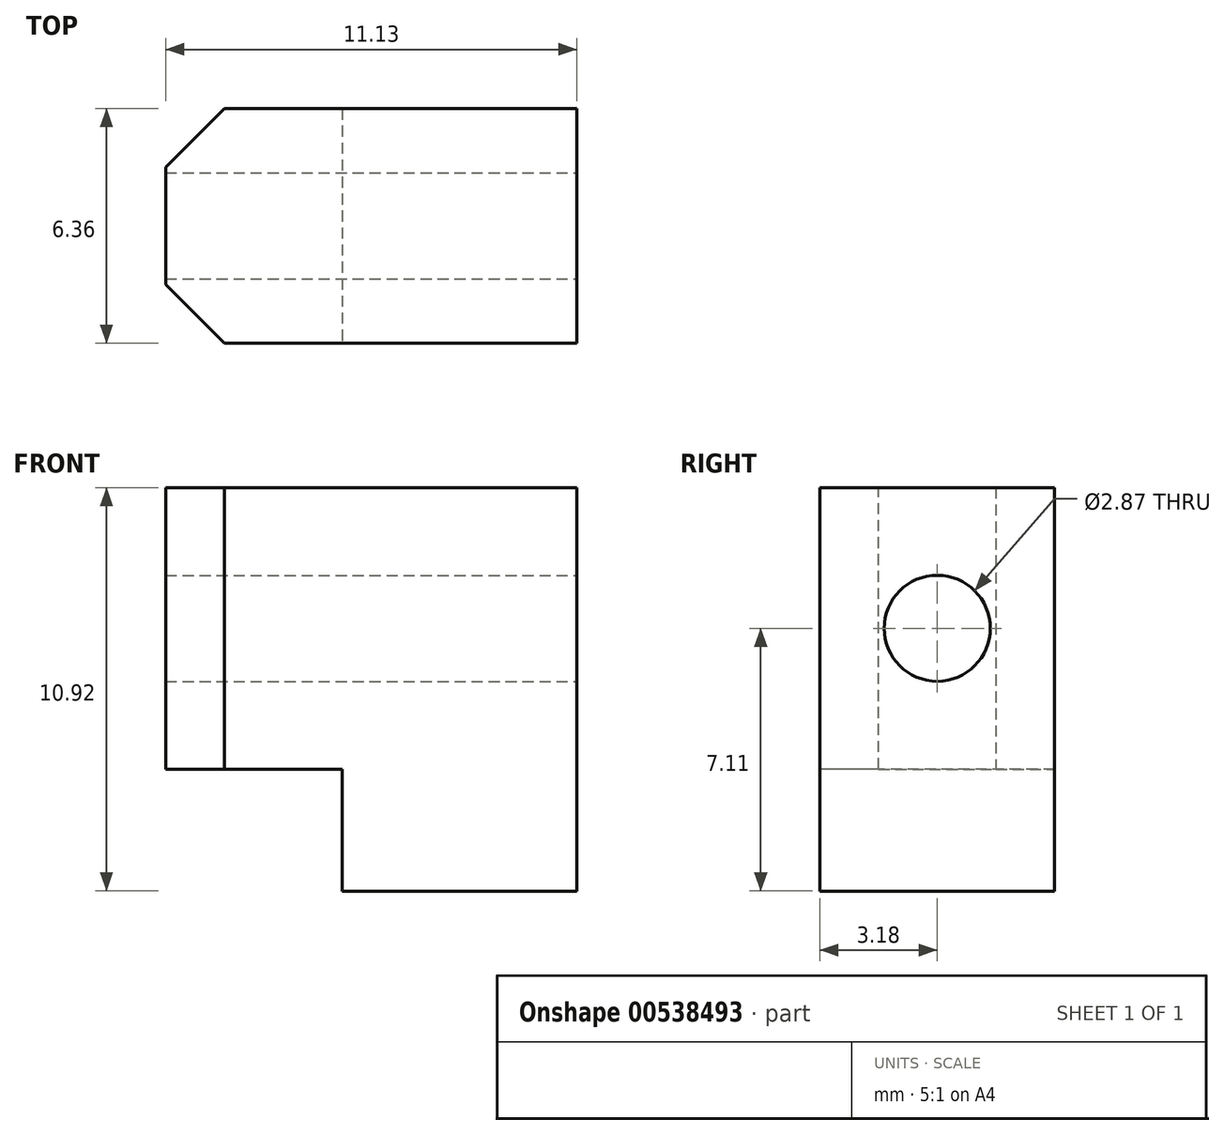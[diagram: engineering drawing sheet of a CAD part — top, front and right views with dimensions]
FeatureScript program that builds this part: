
annotation { "Feature Type Name" : "Feature", "Feature Type Description" : "" }
export const myFeature = defineFeature(function(context is Context, id is Id, definition is map)
    precondition{}
    {
        {
            var Q0;
            Q0=qCreatedBy(makeId("Top.planeOp"),FACE);
            var sketch = newSketch(context, id + "F0", { "sketchPlane" : qUnion([Q0])});
            skLineSegment(sketch, "E0.bottom", {"start": v(0.74, 3.17) * mm, "end": v(7.09, 3.18) * mm});
            skLineSegment(sketch, "E0.top", {"start": v(0.74, -3.18) * mm, "end": v(7.09, -3.17) * mm});
            skLineSegment(sketch, "E0.left", {"start": v(0.74, 3.17) * mm, "end": v(0.74, -3.18) * mm});
            skLineSegment(sketch, "E0.right", {"start": v(7.09, 3.18) * mm, "end": v(7.09, -3.17) * mm});
            skSolve(sketch);
        }
        {
            var Q0;
            Q0=makeQuery(id+"F0.imprint","IMPRINT",FACE,{"disambiguationData":[TD([[makeQuery(id+"F0.imprint","IMPRINT",EDGE,{"derivedFrom":sQuery(id+"F0.wireOp",EDGE,"E0.bottom")}),-1.0]])]});
            extrude(context, id + "F1", {"entities" : qUnion([Q0]), "oppositeDirection" : true, "depth" : 3.3 * mm, "offsetDistance" : 25.4 * mm});
        }
        {
            var Q0;
            Q0=qCreatedBy(makeId("Front.planeOp"),FACE);
            var sketch = newSketch(context, id + "F2", { "sketchPlane" : qUnion([Q0])});
            skLineSegment(sketch, "E1.bottom", {"start": v(7.09, 0) * mm, "end": v(-4.04, 0) * mm});
            skLineSegment(sketch, "E1.top", {"start": v(7.09, 7.62) * mm, "end": v(-4.04, 7.62) * mm});
            skLineSegment(sketch, "E1.left", {"start": v(7.09, 0) * mm, "end": v(7.09, 7.62) * mm});
            skLineSegment(sketch, "E1.right", {"start": v(-4.04, 0) * mm, "end": v(-4.04, 7.62) * mm});
            skSolve(sketch);
        }
        {
            var Q0;
            Q0 = qSketchRegion(id + "F2", true);
            extrude(context, id + "F3", {"entities" : qUnion([Q0]), "operationType" : NewBodyOperationType.ADD, "endBound" : BoundingType.SYMMETRIC, "depth" : 6.35 * mm, "offsetDistance" : 25.4 * mm});
        }
        {
            var Q0;
            Q0=makeQuery(id+"F3.boolean.opBoolean","MERGE",FACE,{"derivedFrom":[makeQuery(id+"F1.opExtrude","SWEPT_FACE",FACE,{"disambiguationData":[OSD([sQuery(id+"F0.wireOp",EDGE,"E0.right")])]}),makeQuery(id+"F3.opExtrude","SWEPT_FACE",FACE,{"disambiguationData":[OSD([sQuery(id+"F2.wireOp",EDGE,"E1.left")])]})]});
            var sketch = newSketch(context, id + "F4", { "sketchPlane" : qUnion([Q0])});
            skCircle(sketch, "E2", {"center": v(0, 3.81) * mm, "radius": 1.44 * mm});
            skSolve(sketch);
        }
        {
            var Q0;
            Q0=makeQuery(id+"F4.imprint","IMPRINT",FACE,{"disambiguationData":[TD([[makeQuery(id+"F4.imprint","IMPRINT",EDGE,{"derivedFrom":sQuery(id+"F4.wireOp",EDGE,"E2")}),1.0]])]});
            extrude(context, id + "F5", {"entities" : qUnion([Q0]), "operationType" : NewBodyOperationType.REMOVE, "endBound" : BoundingType.THROUGH_ALL, "oppositeDirection" : true, "depth" : 25.4 * mm, "offsetDistance" : 25.4 * mm});
        }
        {
            var Q0;
            Q0=makeQuery(id+"F3.opExtrude","CAP_EDGE",EDGE,{"disambiguationData":[OSD([sQuery(id+"F2.wireOp",EDGE,"E1.right")])],"isStart":false});
            var Q1;
            Q1=makeQuery(id+"F3.opExtrude","CAP_EDGE",EDGE,{"disambiguationData":[OSD([sQuery(id+"F2.wireOp",EDGE,"E1.right")])],"isStart":true});
            chamfer(context, id + "F6", {"entities" : qUnion([Q0, Q1]), "width" : 1.59 * mm, "tangentPropagation" : true});
        }
    });
